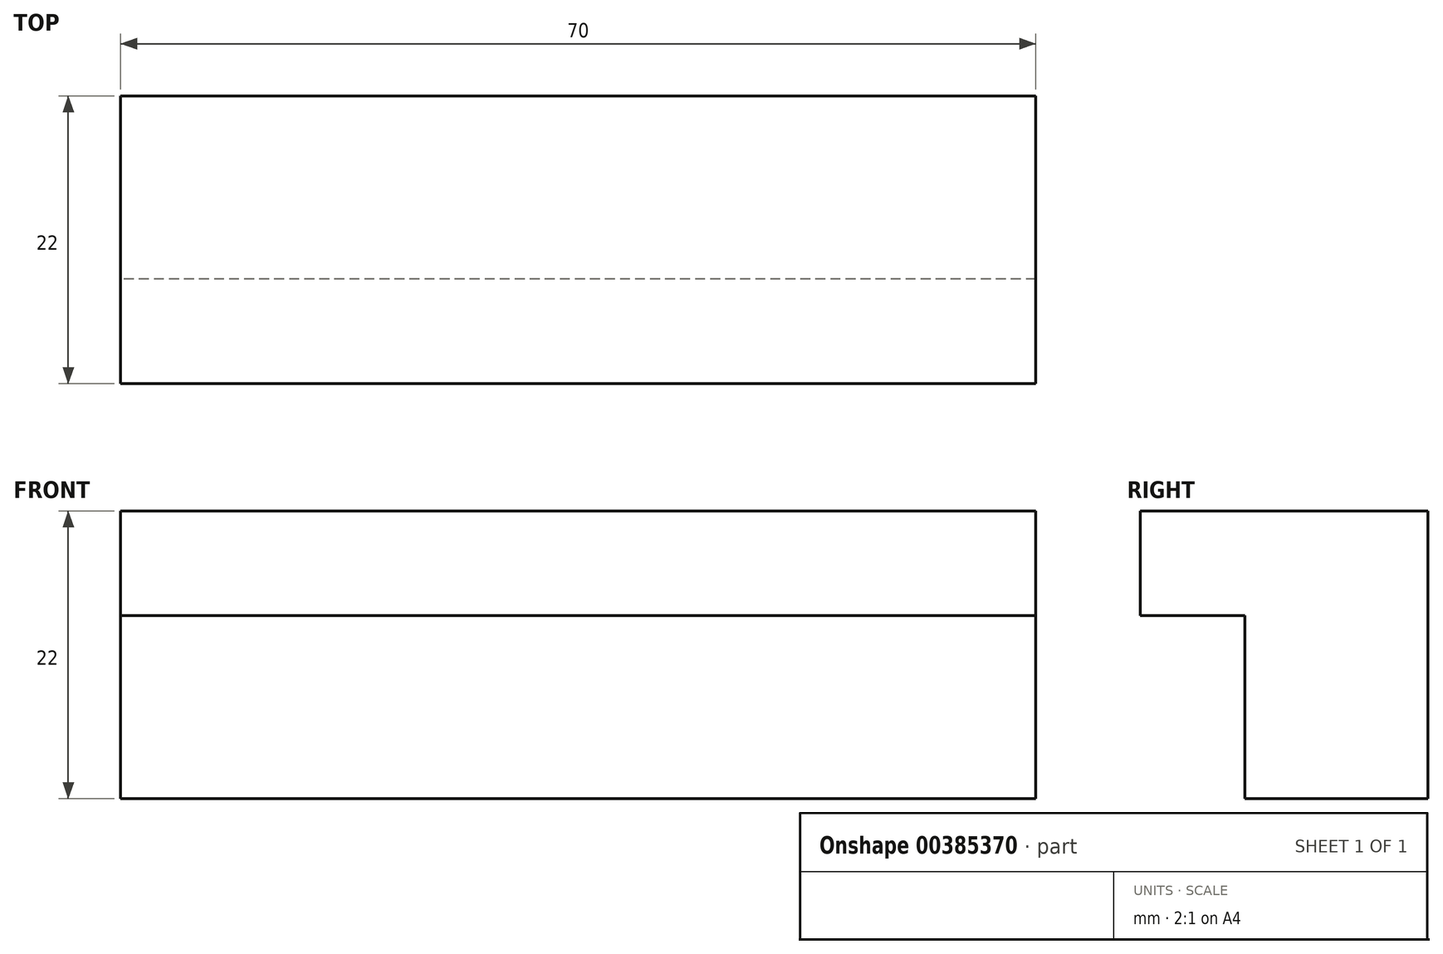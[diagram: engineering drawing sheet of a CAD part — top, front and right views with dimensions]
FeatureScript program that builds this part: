
annotation { "Feature Type Name" : "Feature", "Feature Type Description" : "" }
export const myFeature = defineFeature(function(context is Context, id is Id, definition is map)
    precondition{}
    {
        {
            var Q0;
            Q0=qCreatedBy(makeId("Right.planeOp"),FACE);
            var sketch = newSketch(context, id + "F0", { "sketchPlane" : qUnion([Q0])});
            skLineSegment(sketch, "E0", {"start": v(0, 0) * mm, "end": v(-22, 0) * mm});
            skLineSegment(sketch, "E1", {"start": v(-22, 0) * mm, "end": v(-22, -8) * mm});
            skLineSegment(sketch, "E2", {"start": v(0, 0) * mm, "end": v(0, -22) * mm});
            skLineSegment(sketch, "E3", {"start": v(0, -22) * mm, "end": v(-14, -22) * mm});
            skLineSegment(sketch, "E4", {"start": v(-14, -22) * mm, "end": v(-14, -8) * mm});
            skLineSegment(sketch, "E5", {"start": v(-14, -8) * mm, "end": v(-22, -8) * mm});
            skSolve(sketch);
        }
        {
            var Q0;
            Q0=makeQuery(id+"F0.imprint","IMPRINT",FACE,{"disambiguationData":[TD([[makeQuery(id+"F0.imprint","IMPRINT",EDGE,{"derivedFrom":sQuery(id+"F0.wireOp",EDGE,"E0")}),1.0]])]});
            extrude(context, id + "F1", {"entities" : qUnion([Q0]), "depth" : 70 * mm});
        }
    });
